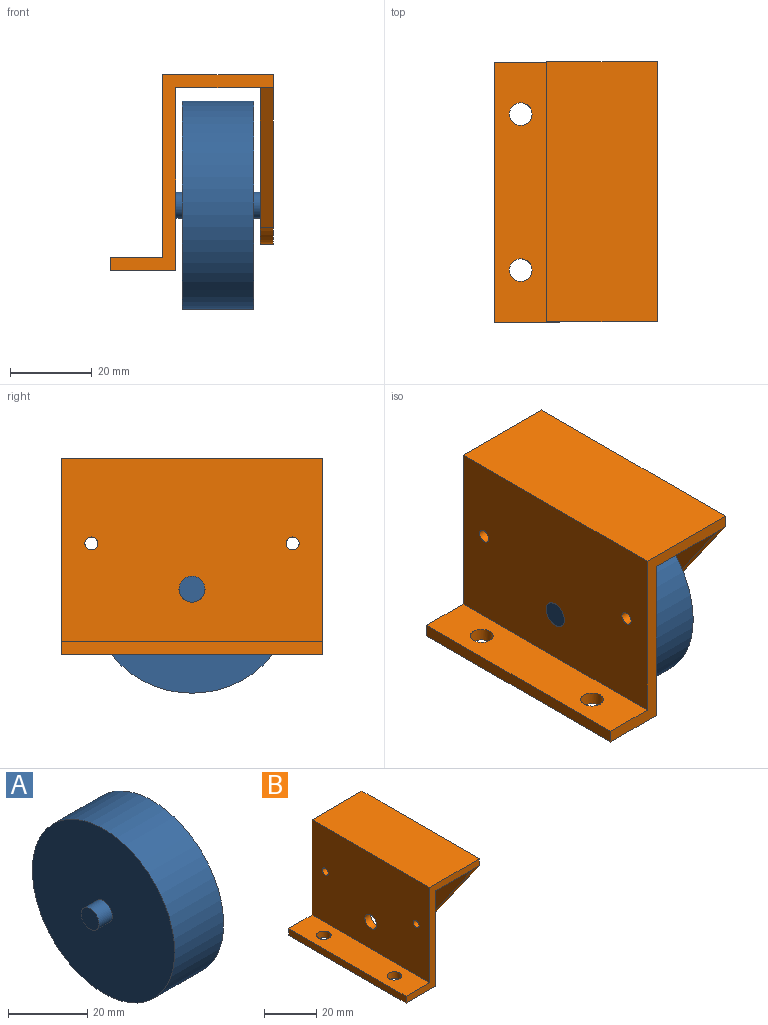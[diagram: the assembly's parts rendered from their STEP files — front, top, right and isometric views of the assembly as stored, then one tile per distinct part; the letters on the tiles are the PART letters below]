
ASSEMBLY  parts=2 mates=1
PART A: 7 faces, bbox 27x50.8x50.8 mm
  f0: cylinder r=3.17mm len=6.35mm, axis (1,0,0), area 95.3mm2, adj f1,f6
  f1: plane 6.35x6.35mm, normal (-1,0,0), area 31.7mm2, adj f0
  f2: cylinder r=3.17mm len=6.35mm, axis (-1,0,0), area 95.3mm2, adj f3,f5
  f3: plane 6.35x6.35mm, normal (1,0,0), area 31.7mm2, adj f2
  f4: cylinder r=25.4mm len=50.8mm, axis (-1,0,0), area 2788.9mm2, adj f5,f6
  f5: plane 50.8x50.8mm, normal (1,0,0), area 1995.2mm2, adj f2,f4
  f6: plane 50.8x50.8mm, normal (-1,0,0), area 1995.2mm2, adj f0,f4
PART B: 20 faces, bbox 39.7x63.5x47.7 mm
  f0: plane 63.5x44.53mm, normal (1,0,0), area 2779.9mm2, adj f2,f4,f7,f8,f15,f16,f17
  f1: plane 63.5x44.53mm, normal (-1,0,0), area 2779.9mm2, adj f2,f4,f5,f10,f15,f16,f17
  f2: plane 47.7x39.69mm, normal (0,-1,0), area 267.4mm2, adj f0,f1,f3,f5,f6,f7,f8,f10
  f3: plane 63.5x41.35mm, normal (1,0,0), area 1563.7mm2, adj f2,f4,f10,f11,f12,f13,f14
  f4: plane 47.7x39.69mm, normal (0,1,0), area 267.4mm2, adj f0,f1,f3,f5,f6,f7,f8,f10
  f5: plane 63.5x12.7mm, normal (0,0,1), area 758.6mm2, adj f1,f2,f4,f6,f18,f19
  f6: plane 63.5x3.18mm, normal (-1,0,0), area 201.6mm2, adj f2,f4,f5,f7
  f7: plane 63.5x15.88mm, normal (0,0,-1), area 960.2mm2, adj f0,f2,f4,f6,f18,f19
  f8: plane 63.5x20.64mm, normal (0,0,-1), area 1310.5mm2, adj f0,f2,f4,f9
  f9: plane 63.5x38.18mm, normal (-1,0,0), area 1362.1mm2, adj f8,f11,f12,f13,f14
  f10: plane 63.5x26.99mm, normal (0,0,1), area 1713.7mm2, adj f1,f2,f3,f4
  f11: cylinder r=3.17mm len=6.35mm, axis (1,0,0), area 63.3mm2, adj f3,f9
  f12: plane 34.12x23.95mm, normal (0,0.82,-0.57), area 132.4mm2, adj f3,f4,f9,f13
  f13: cylinder r=9.53mm len=15.59mm, axis (1,0,0), area 58mm2, adj f3,f9,f12,f14
  f14: plane 34.12x23.95mm, normal (0,-0.82,-0.57), area 132.4mm2, adj f2,f3,f9,f13
  f15: cylinder r=3.17mm len=6.35mm, axis (1,0,0), area 63.3mm2, adj f0,f1
  f16: cylinder r=1.59mm len=3.18mm, axis (1,0,0), area 31.7mm2, adj f0,f1
  f17: cylinder r=1.59mm len=3.18mm, axis (1,0,0), area 31.7mm2, adj f0,f1
  f18: cylinder r=2.76mm len=5.52mm, axis (0,0,-1), area 55.1mm2, adj f5,f7
  f19: cylinder r=2.76mm len=5.52mm, axis (0,0,-1), area 55.1mm2, adj f5,f7
PLACE A t=(56.19,0,0)mm
PLACE B t=(56.22,0,0)mm
MATE cylindrical B.f11 <-> A.f0  axis (1,0,0) through (78.44,0,25.4)mm
